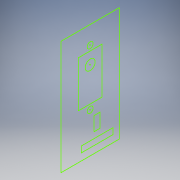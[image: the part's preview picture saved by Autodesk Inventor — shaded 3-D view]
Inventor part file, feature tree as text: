
AUTODESK INVENTOR PART (.ipt)
format: ipt  version: 2018 (Build 220112000, 112)  size: 91,136 bytes
history: native  units: mm
features: sketch x1
ambient origin geometry x8: Origin, YZ Plane, XZ Plane, XY Plane, X Axis, Y Axis, Z Axis, Center Point
feature tree (1):
  sketch  "Boceto1"
